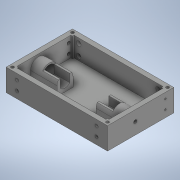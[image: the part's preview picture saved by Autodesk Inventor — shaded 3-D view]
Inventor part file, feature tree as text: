
AUTODESK INVENTOR PART (.ipt)
format: ipt  version: 2020 (Build 240168000, 168)  size: 713,216 bytes
history: native  units: in
note: dims shown in document units (in); Inventor stores cm internally (conversion verified against a paired STEP export)
features: projected_geometry x16, extrude x11, sketch x8, mirror x3
ambient origin geometry x8: Origin, YZ Plane, XZ Plane, XY Plane, X Axis, Y Axis, Z Axis, Center Point
bodies: Solid1 (feature_tree)
feature tree (38):
  extrude  "Extrusion1"  Depth=3.3465in
  extrude  "Extrusion2"  Depth=0.993in TaperAngle=0.0deg
  extrude  "Extrusion5"  Depth=0.0787in
  extrude  "Extrusion6"  Depth=0.7874in TaperAngle=0.0deg
  extrude  "Extrusion7"  Depth=4.6457in
  mirror  "Mirror2"
  extrude  "Extrusion24"  Depth=2.874in
  extrude  "Extrusion25"  Depth=0.2402in
  extrude  "Extrusion26"  Depth=0.0906in
  mirror  "Mirror11"
  extrude  "Extrusion27"  [1 undecoded]
  extrude  "Extrusion28"  Depth=1.9488in
  extrude  "Extrusion29"  Depth=1.9488in
  mirror  "Mirror13"
  sketch  "Sketch1"  dims[d0=5.1181in d1=3.3465in]
  sketch  "Sketch2"  dims[d2=0.1181in d3=0.0in d5=0.993in d6=0.0in]
  projected_geometry  "Projected Loop1"
  projected_geometry  "Projected Loop5"
  sketch  "Sketch9"  dims[d18=0.5906in d20=0.0787in]
  sketch  "Sketch28"  dims[d21=0.5512in d22=0.0in d25=0.7874in d26=0.0in]
  projected_geometry  "Projected Loop15"
  sketch  "Sketch29"  dims[d30=0.4626in d31=0.0in d36=4.6457in]
  projected_geometry  "Projected Loop16"
  projected_geometry  "Projected Loop17"
  projected_geometry  "Projected Loop18"
  projected_geometry  "Projected Loop19"
  sketch  "Sketch30"  dims[d37=2.874in d120=0.2402in]
  projected_geometry  "Projected Loop20"
  projected_geometry  "Projected Loop21"
  projected_geometry  "Projected Loop22"
  sketch  "Sketch32"  dims[d121=0.2402in d122=0.2402in]
  projected_geometry  "Projected Loop23"
  projected_geometry  "Projected Loop24"
  sketch  "Sketch33"  dims[d123=0.2402in d124=0.0906in d125=-0.2233in d126=0.122in d127=0.122in d128=0.122in d129=0.122in d130=2.2126in d131=0.0in d132=0.245in d133=0.1969in d139=0.1496in d140=0.2756in d141=0.0in d145=0.6102in d146=0.6102in d147=0.4803in d148=0.1654in d152=0.1575in d153=0.2843in d154=0.1575in d156=0.0866in d157=0.0in d158=0.0866in d159=0.0866in d160=0.0906in d161=0.0in d163=0.1575in d164=0.1575in d165=0.2843in d166=0.2362in d167=0.0866in d168=0.0in d173=0.315in d176=0.315in d177=0.315in d178=0.315in d179=0.315in d180=0.315in d181=0.5512in d182=0.4331in d183=1.9488in d50=0.0197in d51=0.0344in d52=0.0197in d53=0.0344in d73=0.0197in d74=0.0344in d75=0.0197in d76=0.0344in]
  projected_geometry  "Projected Loop25"
  projected_geometry  "Projected Loop28"
  projected_geometry  "Projected Loop29"
  projected_geometry  "Projected Loop30"
note: 1 required parameter value undecoded (feature->parameter linkage not recoverable at this tier; creation-order binding heuristic only, values carry confidence <= 0.55)
